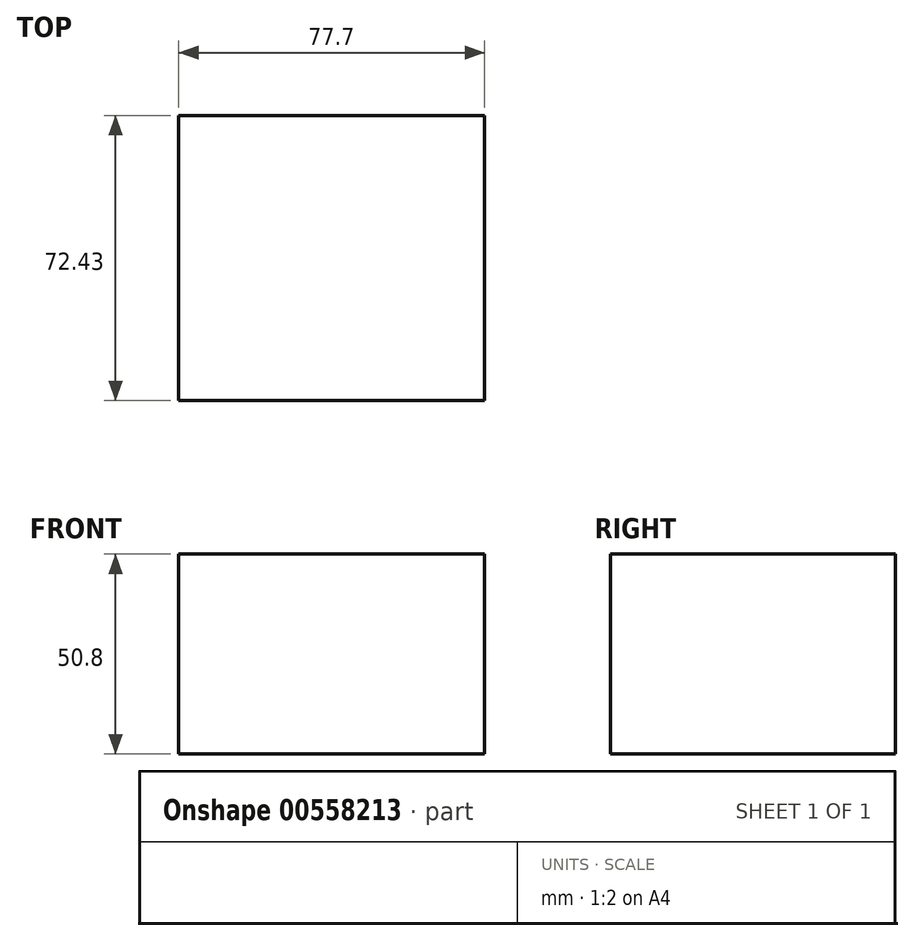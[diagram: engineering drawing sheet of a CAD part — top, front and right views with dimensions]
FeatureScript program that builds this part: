
annotation { "Feature Type Name" : "Feature", "Feature Type Description" : "" }
export const myFeature = defineFeature(function(context is Context, id is Id, definition is map)
    precondition{}
    {
        {
            var Q0;
            Q0=qCreatedBy(makeId("Top.planeOp"),FACE);
            var sketch = newSketch(context, id + "F0", { "sketchPlane" : qUnion([Q0])});
            skLineSegment(sketch, "E0.bottom", {"start": v(-46.58, 46.2) * mm, "end": v(31.12, 46.2) * mm});
            skLineSegment(sketch, "E0.top", {"start": v(-46.58, -26.24) * mm, "end": v(31.12, -26.24) * mm});
            skLineSegment(sketch, "E0.left", {"start": v(-46.58, 46.2) * mm, "end": v(-46.58, -26.24) * mm});
            skLineSegment(sketch, "E0.right", {"start": v(31.12, 46.2) * mm, "end": v(31.12, -26.24) * mm});
            skSolve(sketch);
        }
        {
            var Q0;
            Q0=makeQuery(id+"F0.imprint","IMPRINT",FACE,{"disambiguationData":[TD([[makeQuery(id+"F0.imprint","IMPRINT",EDGE,{"derivedFrom":sQuery(id+"F0.wireOp",EDGE,"E0.bottom")}),-1.0]])]});
            extrude(context, id + "F1", {"entities" : qUnion([Q0]), "depth" : 50.8 * mm, "offsetDistance" : 25.4 * mm});
        }
    });
